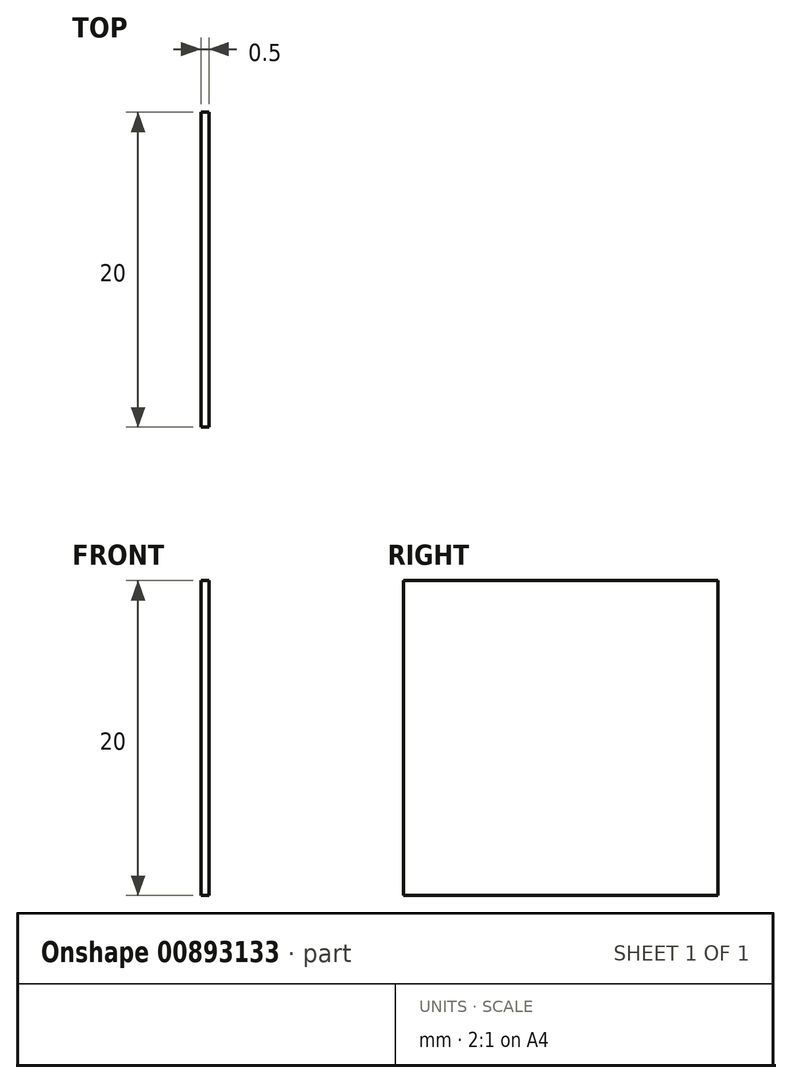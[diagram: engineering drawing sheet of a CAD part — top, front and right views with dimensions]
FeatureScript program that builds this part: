
annotation { "Feature Type Name" : "Feature", "Feature Type Description" : "" }
export const myFeature = defineFeature(function(context is Context, id is Id, definition is map)
    precondition{}
    {
        {
            var Q0;
            Q0=qCreatedBy(makeId("Right.planeOp"),FACE);
            var sketch = newSketch(context, id + "F0", { "sketchPlane" : qUnion([Q0])});
            skLineSegment(sketch, "E0.bottom", {"start": v(0, 0) * mm, "end": v(20, 0) * mm});
            skLineSegment(sketch, "E0.top", {"start": v(0, -20) * mm, "end": v(20, -20) * mm});
            skLineSegment(sketch, "E0.left", {"start": v(0, 0) * mm, "end": v(0, -20) * mm});
            skLineSegment(sketch, "E0.right", {"start": v(20, 0) * mm, "end": v(20, -20) * mm});
            skSolve(sketch);
        }
        {
            var Q0;
            Q0=makeQuery(id+"F0.imprint","IMPRINT",FACE,{"disambiguationData":[TD([[makeQuery(id+"F0.imprint","IMPRINT",EDGE,{"derivedFrom":sQuery(id+"F0.wireOp",EDGE,"E0.bottom")}),-1.0]])]});
            extrude(context, id + "F1", {"entities" : qUnion([Q0]), "depth" : .5 * mm, "offsetDistance" : 25 * mm});
        }
    });
